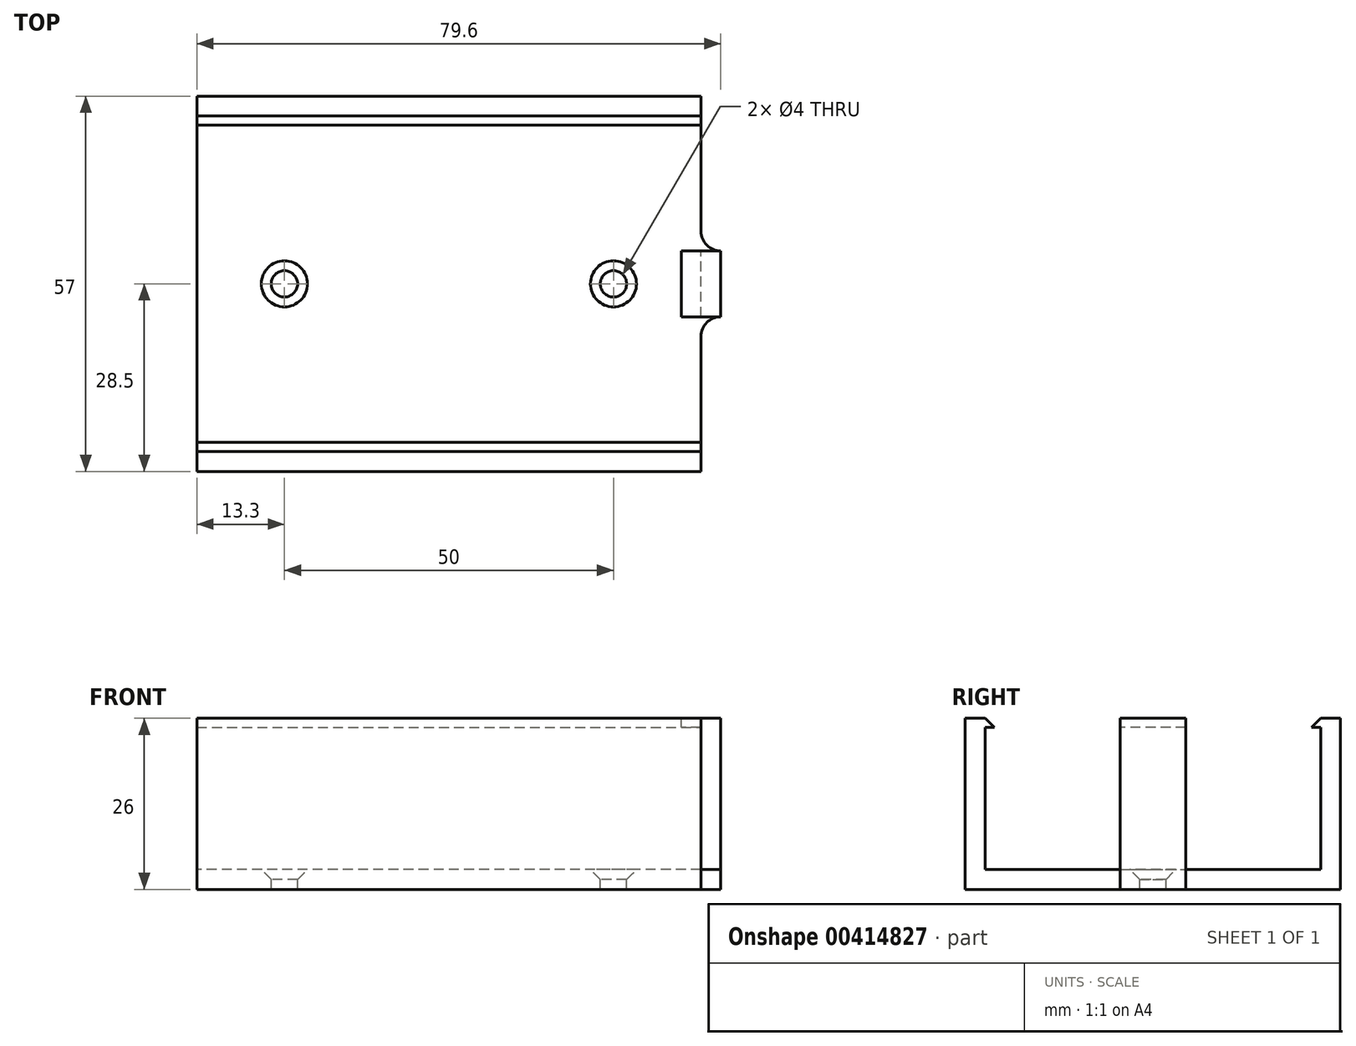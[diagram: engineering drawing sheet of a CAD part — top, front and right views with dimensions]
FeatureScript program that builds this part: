
annotation { "Feature Type Name" : "Feature", "Feature Type Description" : "" }
export const myFeature = defineFeature(function(context is Context, id is Id, definition is map)
    precondition{}
    {
        {
            var Q0;
            Q0=qCreatedBy(makeId("Right.planeOp"),FACE);
            var sketch = newSketch(context, id + "F0", { "sketchPlane" : qUnion([Q0])});
            skLineSegment(sketch, "E0.bottom", {"start": v(-25.5, -10) * mm, "end": v(-5, -10) * mm});
            skLineSegment(sketch, "E0.top", {"start": v(-25.5, 10) * mm, "end": v(-5, 10) * mm});
            skLineSegment(sketch, "E0.left", {"start": v(-25.5, -10) * mm, "end": v(-25.5, 10) * mm});
            skLineSegment(sketch, "E0.right", {"start": v(25.5, -10) * mm, "end": v(25.5, 10) * mm});
            skPoint(sketch, "E0.middle", {"position": v(0, 0) * mm});
            skLineSegment(sketch, "E1.0", {"start": v(-28.5, -13) * mm, "end": v(-28.5, 13) * mm});
            skLineSegment(sketch, "E1.1", {"start": v(-28.5, -13) * mm, "end": v(28.5, -13) * mm});
            skLineSegment(sketch, "E1.2", {"start": v(28.5, -13) * mm, "end": v(28.5, 13) * mm});
            skLineSegment(sketch, "E1.3", {"start": v(-28.5, 13) * mm, "end": v(28.5, 13) * mm});
            skLineSegment(sketch, "E2", {"start": v(0, -13) * mm, "end": v(-5, -13) * mm});
            skLineSegment(sketch, "E3", {"start": v(5, 13) * mm, "end": v(-5, 13) * mm});
            skLineSegment(sketch, "E4", {"start": v(-5, -13) * mm, "end": v(5, -13) * mm});
            skLineSegment(sketch, "E5.trimOffspring", {"start": v(5, -10) * mm, "end": v(25.5, -10) * mm});
            skLineSegment(sketch, "E6.trimOffspring", {"start": v(5, 10) * mm, "end": v(25.5, 10) * mm});
            skLineSegment(sketch, "E7", {"start": v(5, -10) * mm, "end": v(-5, -10) * mm});
            skLineSegment(sketch, "E8", {"start": v(-5, 10) * mm, "end": v(5, 10) * mm});
            skSolve(sketch);
        }
        {
            var Q0;
            Q0 = qSketchRegion(id + "F0", true);
            extrude(context, id + "F1", {"entities" : qUnion([Q0]), "endBound" : BoundingType.SYMMETRIC, "depth" : 76.6 * mm});
        }
        {
            var Q0;
            Q0=makeQuery(id+"F1.opExtrude","SWEPT_FACE",FACE,{"disambiguationData":[OSD([sQuery(id+"F0.wireOp",EDGE,"E1.3"),sQuery(id+"F0.wireOp",EDGE,"E3")])]});
            var sketch = newSketch(context, id + "F2", { "sketchPlane" : qUnion([Q0])});
            skLineSegment(sketch, "E9.bottom", {"start": v(-38.3, -25.5) * mm, "end": v(38.3, -25.5) * mm});
            skLineSegment(sketch, "E9.top", {"start": v(-38.3, 25.5) * mm, "end": v(38.3, 25.5) * mm});
            skLineSegment(sketch, "E9.left", {"start": v(-38.3, -25.5) * mm, "end": v(-38.3, 25.5) * mm});
            skLineSegment(sketch, "E9.right", {"start": v(38.3, -25.5) * mm, "end": v(38.3, 25.5) * mm});
            skPoint(sketch, "E9.middle", {"position": v(0, 0) * mm});
            skSolve(sketch);
        }
        {
            var Q0;
            Q0 = qSketchRegion(id + "F2", true);
            extrude(context, id + "F3", {"entities" : qUnion([Q0]), "operationType" : NewBodyOperationType.REMOVE, "oppositeDirection" : true, "depth" : 19.6 * mm});
        }
        {
            var Q0;
            Q0=makeQuery(id+"F1.opExtrude","CAP_FACE",FACE,{"disambiguationData":[OSD([sQuery(id+"F0.wireOp",EDGE,"E0.bottom"),sQuery(id+"F0.wireOp",EDGE,"E0.top"),sQuery(id+"F0.wireOp",EDGE,"E0.left"),sQuery(id+"F0.wireOp",EDGE,"E0.right"),sQuery(id+"F0.wireOp",EDGE,"E1.0"),sQuery(id+"F0.wireOp",EDGE,"E1.1"),sQuery(id+"F0.wireOp",EDGE,"E1.2"),sQuery(id+"F0.wireOp",EDGE,"E1.3"),sQuery(id+"F0.wireOp",EDGE,"E3"),sQuery(id+"F0.wireOp",EDGE,"E4"),sQuery(id+"F0.wireOp",EDGE,"E5.trimOffspring"),sQuery(id+"F0.wireOp",EDGE,"E6.trimOffspring"),sQuery(id+"F0.wireOp",EDGE,"E7"),sQuery(id+"F0.wireOp",EDGE,"E8")])],"isStart":false});
            var sketch = newSketch(context, id + "F4", { "sketchPlane" : qUnion([Q0])});
            skLineSegment(sketch, "E10", {"start": v(-25.5, 13) * mm, "end": v(-24.09, 11.59) * mm});
            skLineSegment(sketch, "E11", {"start": v(-24.09, 11.59) * mm, "end": v(-25.5, 11.59) * mm});
            skLineSegment(sketch, "E12", {"start": v(25.5, 13) * mm, "end": v(24.09, 11.59) * mm});
            skLineSegment(sketch, "E13", {"start": v(24.09, 11.59) * mm, "end": v(25.5, 11.59) * mm});
            skSolve(sketch);
        }
        {
            var Q0;
            {var subQ0=sQuery(id+"F4.wireOp",EDGE,"E12");Q0=makeQuery(id+"F4.imprint","IMPRINT",FACE,{"disambiguationData":[TD([[makeQuery(id+"F4.imprint","IMPRINT",EDGE,{"derivedFrom":subQ0}),1.0]])]});}
            var Q1;
            {var subQ0=sQuery(id+"F4.wireOp",EDGE,"E10");Q1=makeQuery(id+"F4.imprint","IMPRINT",FACE,{"disambiguationData":[TD([[makeQuery(id+"F4.imprint","IMPRINT",EDGE,{"derivedFrom":subQ0}),-1.0]])]});}
            extrude(context, id + "F5", {"entities" : qUnion([Q0, Q1]), "operationType" : NewBodyOperationType.ADD, "oppositeDirection" : true, "depth" : 76.6 * mm});
        }
        {
            var Q0;
            {var subQ0=sQuery(id+"F2.wireOp",EDGE,"E9.right");var subQ1=sQuery(id+"F0.wireOp",EDGE,"E3");var subQ2=sQuery(id+"F0.wireOp",EDGE,"E1.3");var subQ3=sQuery(id+"F0.wireOp",EDGE,"E0.right");var subQ4=sQuery(id+"F0.wireOp",EDGE,"E0.left");Q0=makeQuery(id+"F5.boolean.opBoolean","MERGE",FACE,{"derivedFrom":[makeQuery(id+"F1.opExtrude","CAP_FACE",FACE,{"disambiguationData":[OSD([sQuery(id+"F0.wireOp",EDGE,"E0.bottom"),sQuery(id+"F0.wireOp",EDGE,"E0.top"),subQ4,subQ3,sQuery(id+"F0.wireOp",EDGE,"E1.0"),sQuery(id+"F0.wireOp",EDGE,"E1.1"),sQuery(id+"F0.wireOp",EDGE,"E1.2"),subQ2,subQ1,sQuery(id+"F0.wireOp",EDGE,"E4"),sQuery(id+"F0.wireOp",EDGE,"E5.trimOffspring"),sQuery(id+"F0.wireOp",EDGE,"E6.trimOffspring"),sQuery(id+"F0.wireOp",EDGE,"E7"),sQuery(id+"F0.wireOp",EDGE,"E8")])],"isStart":false}),makeQuery(id+"F5.opExtrude","CAP_FACE",FACE,{"disambiguationData":[OSD([subQ4,subQ2,subQ1,sQuery(id+"F2.wireOp",EDGE,"E9.bottom"),subQ0,sQuery(id+"F4.wireOp",EDGE,"E10"),sQuery(id+"F4.wireOp",EDGE,"E11")])],"isStart":true}),makeQuery(id+"F5.opExtrude","CAP_FACE",FACE,{"disambiguationData":[OSD([subQ3,subQ2,subQ1,sQuery(id+"F2.wireOp",EDGE,"E9.top"),subQ0,sQuery(id+"F4.wireOp",EDGE,"E12"),sQuery(id+"F4.wireOp",EDGE,"E13")])],"isStart":true})]});}
            var sketch = newSketch(context, id + "F6", { "sketchPlane" : qUnion([Q0])});
            skLineSegment(sketch, "E14", {"start": v(0, 0) * mm, "end": v(0, -13) * mm, "construction": true});
            skLineSegment(sketch, "E15", {"start": v(0, -13) * mm, "end": v(-5, -13) * mm});
            skLineSegment(sketch, "E16", {"start": v(-5, -13) * mm, "end": v(5, -13) * mm});
            skLineSegment(sketch, "E17", {"start": v(-5, -13) * mm, "end": v(-5, 13) * mm});
            skLineSegment(sketch, "E18", {"start": v(-5, 13) * mm, "end": v(5, 13) * mm});
            skLineSegment(sketch, "E19", {"start": v(5, -13) * mm, "end": v(5, 13) * mm});
            skSolve(sketch);
        }
        {
            var Q0;
            Q0 = qSketchRegion(id + "F6", true);
            extrude(context, id + "F7", {"entities" : qUnion([Q0]), "operationType" : NewBodyOperationType.ADD, "endBound" : BoundingType.SYMMETRIC, "depth" : 6 * mm});
        }
        {
            var Q0;
            Q0=makeQuery(id+"F7.opExtrude","CAP_FACE",FACE,{"disambiguationData":[OSD([sQuery(id+"F6.wireOp",EDGE,"E16"),sQuery(id+"F6.wireOp",EDGE,"E17"),sQuery(id+"F6.wireOp",EDGE,"E18"),sQuery(id+"F6.wireOp",EDGE,"E19")])],"isStart":true});
            var sketch = newSketch(context, id + "F8", { "sketchPlane" : qUnion([Q0])});
            skLineSegment(sketch, "E20.left", {"start": v(-5, -10) * mm, "end": v(-5, 11.6) * mm});
            skPoint(sketch, "E20.middle", {"position": v(0, 0) * mm});
            skPoint(sketch, "E20.right.end.orphan", {"position": v(5, 10) * mm});
            skPoint(sketch, "E20.right.start.orphan", {"position": v(5, -11.6) * mm});
            skLineSegment(sketch, "E21", {"start": v(-5, -10) * mm, "end": v(5, -10) * mm});
            skLineSegment(sketch, "E22", {"start": v(-5, 11.6) * mm, "end": v(5, 11.6) * mm});
            skLineSegment(sketch, "E23", {"start": v(5, 11.6) * mm, "end": v(5, -10) * mm});
            skSolve(sketch);
        }
        {
            var Q0;
            Q0 = qSketchRegion(id + "F8", true);
            extrude(context, id + "F9", {"entities" : qUnion([Q0]), "operationType" : NewBodyOperationType.REMOVE, "oppositeDirection" : true, "depth" : 3 * mm});
        }
        {
            var Q0;
            {var subQ0=sQuery(id+"F2.wireOp",EDGE,"E9.right");var subQ1=sQuery(id+"F0.wireOp",EDGE,"E3");var subQ2=sQuery(id+"F0.wireOp",EDGE,"E1.3");var subQ3=sQuery(id+"F0.wireOp",EDGE,"E0.right");var subQ4=sQuery(id+"F0.wireOp",EDGE,"E0.left");Q0=makeQuery(id+"F7.boolean.opBoolean","INTERSECT",EDGE,{"derivedFrom":[makeQuery(id+"F5.boolean.opBoolean","MERGE",FACE,{"derivedFrom":[makeQuery(id+"F1.opExtrude","CAP_FACE",FACE,{"disambiguationData":[OSD([sQuery(id+"F0.wireOp",EDGE,"E0.bottom"),sQuery(id+"F0.wireOp",EDGE,"E0.top"),subQ4,subQ3,sQuery(id+"F0.wireOp",EDGE,"E1.0"),sQuery(id+"F0.wireOp",EDGE,"E1.1"),sQuery(id+"F0.wireOp",EDGE,"E1.2"),subQ2,subQ1,sQuery(id+"F0.wireOp",EDGE,"E4"),sQuery(id+"F0.wireOp",EDGE,"E5.trimOffspring"),sQuery(id+"F0.wireOp",EDGE,"E6.trimOffspring"),sQuery(id+"F0.wireOp",EDGE,"E7"),sQuery(id+"F0.wireOp",EDGE,"E8")])],"isStart":false}),makeQuery(id+"F5.opExtrude","CAP_FACE",FACE,{"disambiguationData":[OSD([subQ4,subQ2,subQ1,sQuery(id+"F2.wireOp",EDGE,"E9.bottom"),subQ0,sQuery(id+"F4.wireOp",EDGE,"E10"),sQuery(id+"F4.wireOp",EDGE,"E11")])],"isStart":true}),makeQuery(id+"F5.opExtrude","CAP_FACE",FACE,{"disambiguationData":[OSD([subQ3,subQ2,subQ1,sQuery(id+"F2.wireOp",EDGE,"E9.top"),subQ0,sQuery(id+"F4.wireOp",EDGE,"E12"),sQuery(id+"F4.wireOp",EDGE,"E13")])],"isStart":true})]}),makeQuery(id+"F7.opExtrude","SWEPT_FACE",FACE,{"disambiguationData":[OSD([sQuery(id+"F6.wireOp",EDGE,"E17")])]})]});}
            var Q1;
            {var subQ0=sQuery(id+"F2.wireOp",EDGE,"E9.right");var subQ1=sQuery(id+"F0.wireOp",EDGE,"E3");var subQ2=sQuery(id+"F0.wireOp",EDGE,"E1.3");var subQ3=sQuery(id+"F0.wireOp",EDGE,"E0.right");var subQ4=sQuery(id+"F0.wireOp",EDGE,"E0.left");Q1=makeQuery(id+"F7.boolean.opBoolean","INTERSECT",EDGE,{"derivedFrom":[makeQuery(id+"F5.boolean.opBoolean","MERGE",FACE,{"derivedFrom":[makeQuery(id+"F1.opExtrude","CAP_FACE",FACE,{"disambiguationData":[OSD([sQuery(id+"F0.wireOp",EDGE,"E0.bottom"),sQuery(id+"F0.wireOp",EDGE,"E0.top"),subQ4,subQ3,sQuery(id+"F0.wireOp",EDGE,"E1.0"),sQuery(id+"F0.wireOp",EDGE,"E1.1"),sQuery(id+"F0.wireOp",EDGE,"E1.2"),subQ2,subQ1,sQuery(id+"F0.wireOp",EDGE,"E4"),sQuery(id+"F0.wireOp",EDGE,"E5.trimOffspring"),sQuery(id+"F0.wireOp",EDGE,"E6.trimOffspring"),sQuery(id+"F0.wireOp",EDGE,"E7"),sQuery(id+"F0.wireOp",EDGE,"E8")])],"isStart":false}),makeQuery(id+"F5.opExtrude","CAP_FACE",FACE,{"disambiguationData":[OSD([subQ4,subQ2,subQ1,sQuery(id+"F2.wireOp",EDGE,"E9.bottom"),subQ0,sQuery(id+"F4.wireOp",EDGE,"E10"),sQuery(id+"F4.wireOp",EDGE,"E11")])],"isStart":true}),makeQuery(id+"F5.opExtrude","CAP_FACE",FACE,{"disambiguationData":[OSD([subQ3,subQ2,subQ1,sQuery(id+"F2.wireOp",EDGE,"E9.top"),subQ0,sQuery(id+"F4.wireOp",EDGE,"E12"),sQuery(id+"F4.wireOp",EDGE,"E13")])],"isStart":true})]}),makeQuery(id+"F7.opExtrude","SWEPT_FACE",FACE,{"disambiguationData":[OSD([sQuery(id+"F6.wireOp",EDGE,"E19")])]})]});}
            fillet(context, id + "F10", {"entities" : qUnion([Q0, Q1]), "radius" : 3 * mm, "tangentPropagation" : true, "allowEdgeOverflow" : false});
        }
        {
            var Q0;
            Q0=makeQuery(id+"F9.boolean.opBoolean","MERGE",FACE,{"derivedFrom":[makeQuery(id+"F1.opExtrude","SWEPT_FACE",FACE,{"disambiguationData":[OSD([sQuery(id+"F0.wireOp",EDGE,"E0.bottom"),sQuery(id+"F0.wireOp",EDGE,"E5.trimOffspring"),sQuery(id+"F0.wireOp",EDGE,"E7")])]}),makeQuery(id+"F9.opExtrude","SWEPT_FACE",FACE,{"disambiguationData":[OSD([sQuery(id+"F8.wireOp",EDGE,"E21")])]})]});
            var sketch = newSketch(context, id + "F11", { "sketchPlane" : qUnion([Q0])});
            skPoint(sketch, "E24.end.orphan", {"position": v(-25, 0) * mm});
            skPoint(sketch, "E25.end.orphan", {"position": v(25, 0) * mm});
            skCircle(sketch, "E26", {"center": v(-25, 0) * mm, "radius": 5 * mm});
            skCircle(sketch, "E27", {"center": v(25, 0) * mm, "radius": 5 * mm});
            skSolve(sketch);
        }
        {
            var Q0;
            Q0=sQuery(id+"F11.wireOp",VERTEX,"E24.end.orphan");
            var Q1;
            Q1=sQuery(id+"F11.wireOp",VERTEX,"E25.end.orphan");
            var Q2;
            Q2=makeQuery(id+"F1.opExtrude","SWEPT_BODY",BODY,{"disambiguationData":[OSD([sQuery(id+"F0.wireOp",EDGE,"E0.bottom"),sQuery(id+"F0.wireOp",EDGE,"E0.top"),sQuery(id+"F0.wireOp",EDGE,"E0.left"),sQuery(id+"F0.wireOp",EDGE,"E0.right"),sQuery(id+"F0.wireOp",EDGE,"E1.0"),sQuery(id+"F0.wireOp",EDGE,"E1.1"),sQuery(id+"F0.wireOp",EDGE,"E1.2"),sQuery(id+"F0.wireOp",EDGE,"E1.3"),sQuery(id+"F0.wireOp",EDGE,"E3"),sQuery(id+"F0.wireOp",EDGE,"E4"),sQuery(id+"F0.wireOp",EDGE,"E5.trimOffspring"),sQuery(id+"F0.wireOp",EDGE,"E6.trimOffspring"),sQuery(id+"F0.wireOp",EDGE,"E7"),sQuery(id+"F0.wireOp",EDGE,"E8")])]});
            hole(context, id + "F12", {"style" : HoleStyle.C_SINK, "endStyle" : HoleEndStyle.THROUGH, "holeDiameter" : 4 * mm, "cSinkDiameter" : 7 * mm, "cSinkAngle" : 90 * degree, "isTappedThrough" : true, "tappedDepth" : 12 * mm, "tapClearance" : 3, "locations" : qUnion([Q0, Q1]), "scope" : qUnion([Q2])});
        }
    });
